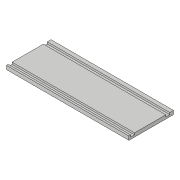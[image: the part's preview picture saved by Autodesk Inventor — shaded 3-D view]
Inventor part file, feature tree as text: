
AUTODESK INVENTOR PART (.ipt)
format: ipt  version: 2018.3 (Build 223284000, 284)  size: 97,792 bytes
history: native  units: in
note: dims shown in document units (in); Inventor stores cm internally (conversion verified against a paired STEP export)
features: extrude x2, sketch x2
ambient origin geometry x8: Origin, YZ Plane, XZ Plane, XY Plane, X Axis, Y Axis, Z Axis, Center Point
bodies: Solid1 (feature_tree)
feature tree (4):
  extrude  "Extrusion1"  Depth=0.125in TaperAngle=0.0deg
  extrude  "Extrusion2"  Depth=0.125in
  sketch  "Sketch1"  dims[d0=4.125in d1=1.5in d2=0.125in d3=0.0in]
  sketch  "Sketch2"  dims[d4=0.135in d5=0.125in d6=0.126in d7=0.0625in d8=0.0625in d9=0.0in]
